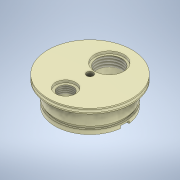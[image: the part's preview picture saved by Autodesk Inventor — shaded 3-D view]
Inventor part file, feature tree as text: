
AUTODESK INVENTOR PART (.ipt)
format: ipt  version: 2020 (Build 240168000, 168)  size: 215,040 bytes
history: native  units: mm
features: sketch x6, hole x4, extrude x2, thread x2, revolve x1
ambient origin geometry x8: Origin, YZ Plane, XZ Plane, XY Plane, X Axis, Y Axis, Z Axis, Center Point
bodies: Solid1 (feature_tree)
feature tree (15):
  revolve  "Revolution1"  [1 undecoded]
  hole  "Hole1"  [1 undecoded]
  hole  "Hole2"  [1 undecoded]
  extrude  "Extrusion2"  TaperAngle=90.0deg  [1 undecoded]
  sketch  "Sketch6"  dims[d17=33.0mm]
  hole  "Hole3"  [1 undecoded]
  hole  "Hole4"  [1 undecoded]
  extrude  "Extrusion3"  Depth=5.05mm
  thread  "Thread1"  [1 undecoded]
  thread  "Thread2"  [1 undecoded]
  sketch  "Sketch1"  dims[d0=33.0mm d1=50.0mm]
  sketch  "Sketch3"  dims[d2=6.0mm d3=41.75mm]
  sketch  "Sketch4"  dims[d4=5.0mm d5=3.7mm]
  sketch  "Sketch5"  dims[d9=39.5mm d10=90.0deg]
  sketch  "Sketch7"  dims[d18=30.0mm d19=12.0mm d20=4.0mm d21=2.0mm d22=90.0deg d23=79.1mm d24=20.594885mm d25=23.0mm d27=29.0mm d28=18.0mm d29=8.0mm d30=4.0mm d31=2.0mm d32=90.0deg d33=53.3mm d34=20.594885mm d35=5.05mm d36=3.0mm d37=10.1mm d38=50.8mm d39=0.0mm d40=5.0mm d41=20.0mm d42=4.0mm d43=2.0mm d44=90.0deg d45=25.0mm d46=20.594885mm d50=8.0mm d51=66.0mm d52=4.0mm d53=2.0mm d54=90.0deg d55=20.0mm d56=20.594885mm d57=24.0mm d58=35.0mm d59=3.0mm d60=0.0mm d61=9.0mm d62=0.0mm d63=12.0mm d64=0.0mm d65=3.0mm d66=1.5mm d67=8.25mm]
note: 8 required parameter values undecoded (feature->parameter linkage not recoverable at this tier; creation-order binding heuristic only, values carry confidence <= 0.55)